# Revit family: Safety_Truck-Restraint_Nova-Tech_TruckLockANCHOR-Cast
name_source: partatom
category: Generic Models
units: mm (PartAtom-declared; Revit-internal decimal feet)

## family parameters
Can host rebar = No
Classification Number = 23.50.70.27
Cut with Voids When Loaded = No
Host = Face
Maintain Annotation Orientation = No
Part Type = Normal
Room Calculation Point = No
Round Connector Dimension = Use Diameter
Shared = No

## types (1)
- Safety_Truck-Restraint_Nova-Tech_TruckLockANCHOR-Cast
    Assembly Code = E1030300
    Core Depth = 2' - 6"
    Default Elevation = 4' - 0"
    Description = Nova Technology Dock Product as Specified
    Expected Lifespan (Years) = 0
    Fixture Material = Metal - Nova - Zinc Coated Steel
    Keynote = 11160
    Maintenance Schedule (Months) = 0
    Manufacturer = Nova Technology
    Manufacturer Fax = 262-502-1511
    Manufacturer Website = http://www.novalocks.com
    Model = As Specified
    Product Data = http://arcat.com
    Revision = R1_4_2013
    Sales Information = http://www.novalocks.com
    Send Message = http://www.arcat.com
    Specification = http://arcat.com
    URL = http://www.novalocks.com
    Unit Depth = 2' - 1 1/32"
    Unit Height = 0' - 10"
    Unit Width = 1' - 3 15/16"
    Warranty Duration (Years) = 0

## geometry (parser evidence)
native form markers: Blend x4, Sweep x3
no freeform markers — native parametric forms only
